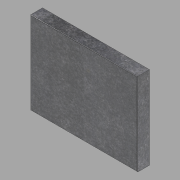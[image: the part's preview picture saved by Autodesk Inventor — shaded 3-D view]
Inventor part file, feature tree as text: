
AUTODESK INVENTOR PART (.ipt)
format: ipt  version: 2022.1 (Build 261234020, 234B)  size: 109,056 bytes
history: native  units: in
note: dims shown in document units (in); Inventor stores cm internally (conversion verified against a paired STEP export)
features: extrude x1, fillet x1, sketch x1
ambient origin geometry x8: Origin, YZ Plane, XZ Plane, XY Plane, X Axis, Y Axis, Z Axis, Center Point
bodies: Solid1 (feature_tree)
feature tree (3):
  extrude  "Extrusion1"  Depth=41.0in
  fillet  "Fillet1"  Radius=6.0in
  sketch  "Sketch1"  dims[d0=53.0in d1=41.0in d2=6.0in d3=0.0in d4=0.25in]
